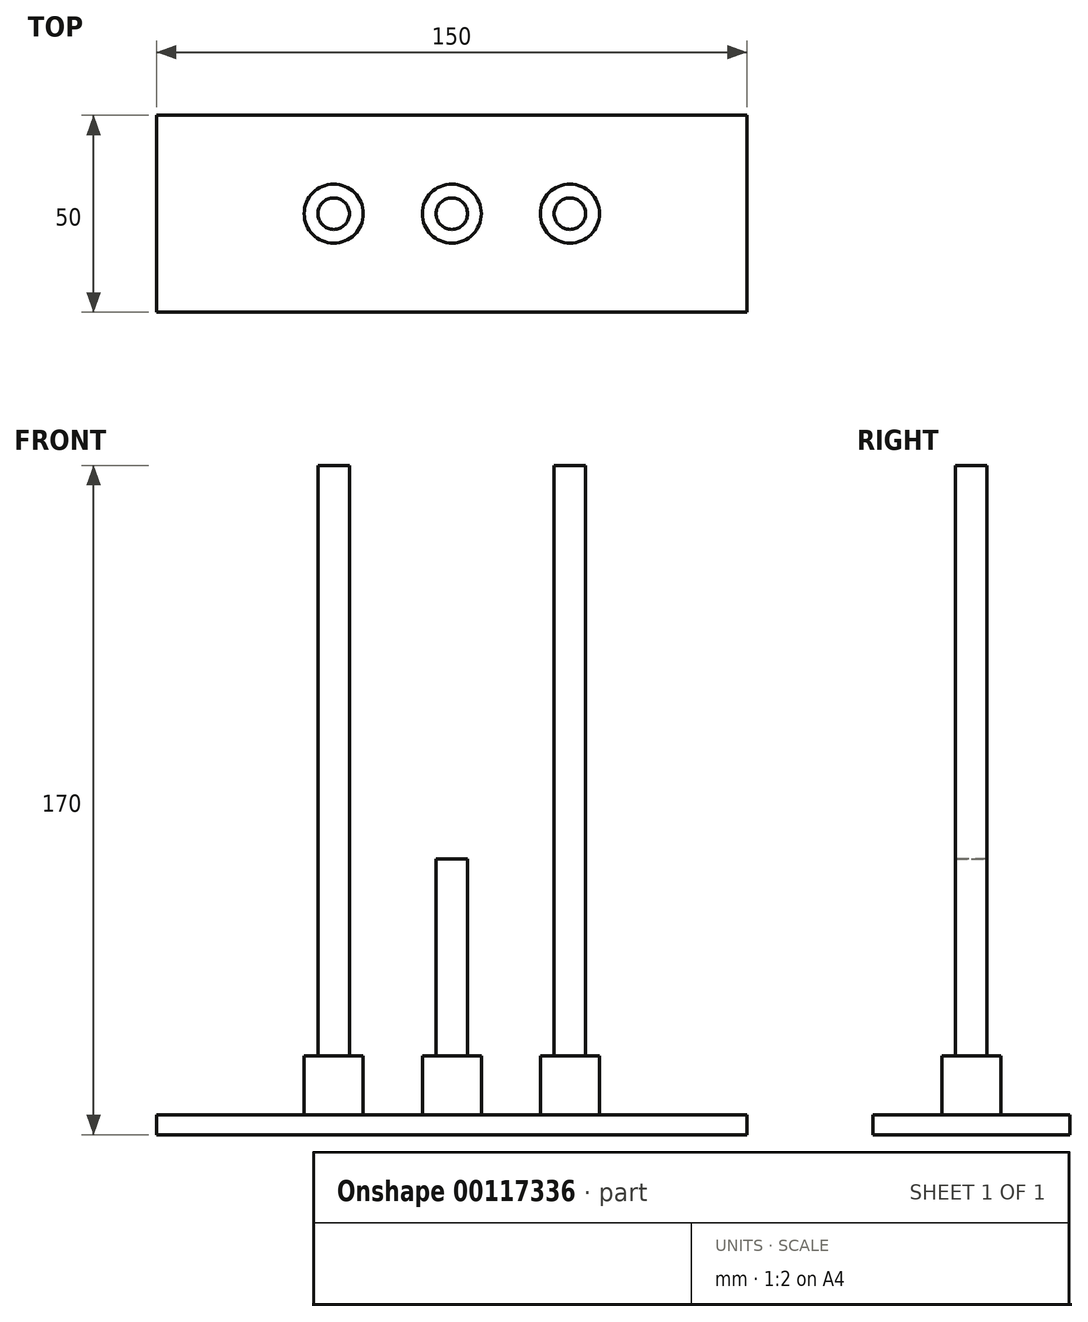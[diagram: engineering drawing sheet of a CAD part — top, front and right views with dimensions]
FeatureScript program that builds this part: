
annotation { "Feature Type Name" : "Feature", "Feature Type Description" : "" }
export const myFeature = defineFeature(function(context is Context, id is Id, definition is map)
    precondition{}
    {
        {
            var Q0;
            Q0=qCreatedBy(makeId("Top.planeOp"),FACE);
            var sketch = newSketch(context, id + "F0", { "sketchPlane" : qUnion([Q0])});
            skLineSegment(sketch, "E0.bottom", {"start": v(0, 0) * mm, "end": v(150, 0) * mm});
            skLineSegment(sketch, "E0.top", {"start": v(0, 50) * mm, "end": v(150, 50) * mm});
            skLineSegment(sketch, "E0.left", {"start": v(0, 0) * mm, "end": v(0, 50) * mm});
            skLineSegment(sketch, "E0.right", {"start": v(150, 0) * mm, "end": v(150, 50) * mm});
            skSolve(sketch);
        }
        {
            var Q0;
            Q0 = qSketchRegion(id + "F0", true);
            extrude(context, id + "F1", {"entities" : qUnion([Q0]), "depth" : 5 * mm});
        }
        {
            var Q0;
            Q0=makeQuery(id+"F1.opExtrude","CAP_FACE",FACE,{"disambiguationData":[OSD([sQuery(id+"F0.wireOp",EDGE,"E0.bottom"),sQuery(id+"F0.wireOp",EDGE,"E0.top"),sQuery(id+"F0.wireOp",EDGE,"E0.left"),sQuery(id+"F0.wireOp",EDGE,"E0.right")])],"isStart":false});
            var sketch = newSketch(context, id + "F2", { "sketchPlane" : qUnion([Q0])});
            skPoint(sketch, "E1.centerSnap0", {"position": v(75, 50) * mm});
            skPoint(sketch, "E1.centerSnap1", {"position": v(0, 25) * mm});
            skCircle(sketch, "E2", {"center": v(45, 25) * mm, "radius": 7.5 * mm});
            skCircle(sketch, "E3.MirrorC", {"center": v(75, 25) * mm, "radius": 7.5 * mm});
            skCircle(sketch, "E4", {"center": v(105, 25) * mm, "radius": 7.5 * mm});
            skSolve(sketch);
        }
        {
            var Q0;
            Q0 = qSketchRegion(id + "F2", true);
            extrude(context, id + "F3", {"entities" : qUnion([Q0]), "operationType" : NewBodyOperationType.ADD, "depth" : 15 * mm});
        }
        {
            var Q0;
            Q0=makeQuery(id+"F3.opExtrude","CAP_FACE",FACE,{"disambiguationData":[OSD([sQuery(id+"F2.wireOp",EDGE,"E3.MirrorC")])],"isStart":false});
            var sketch = newSketch(context, id + "F4", { "sketchPlane" : qUnion([Q0])});
            skCircle(sketch, "E5", {"center": v(45, 25) * mm, "radius": 4 * mm});
            skCircle(sketch, "E6", {"center": v(105, 25) * mm, "radius": 4 * mm});
            skSolve(sketch);
        }
        {
            var Q0;
            Q0 = qSketchRegion(id + "F4", true);
            extrude(context, id + "F5", {"entities" : qUnion([Q0]), "operationType" : NewBodyOperationType.ADD, "depth" : 150 * mm});
        }
        {
            var Q0;
            Q0=makeQuery(id+"F3.opExtrude","CAP_FACE",FACE,{"disambiguationData":[OSD([sQuery(id+"F2.wireOp",EDGE,"E3.MirrorC")])],"isStart":false});
            var sketch = newSketch(context, id + "F6", { "sketchPlane" : qUnion([Q0])});
            skCircle(sketch, "E7", {"center": v(75, 25) * mm, "radius": 4 * mm});
            skSolve(sketch);
        }
        {
            var Q0;
            Q0 = qSketchRegion(id + "F6", true);
            extrude(context, id + "F7", {"entities" : qUnion([Q0]), "operationType" : NewBodyOperationType.ADD, "depth" : 50 * mm});
        }
    });
